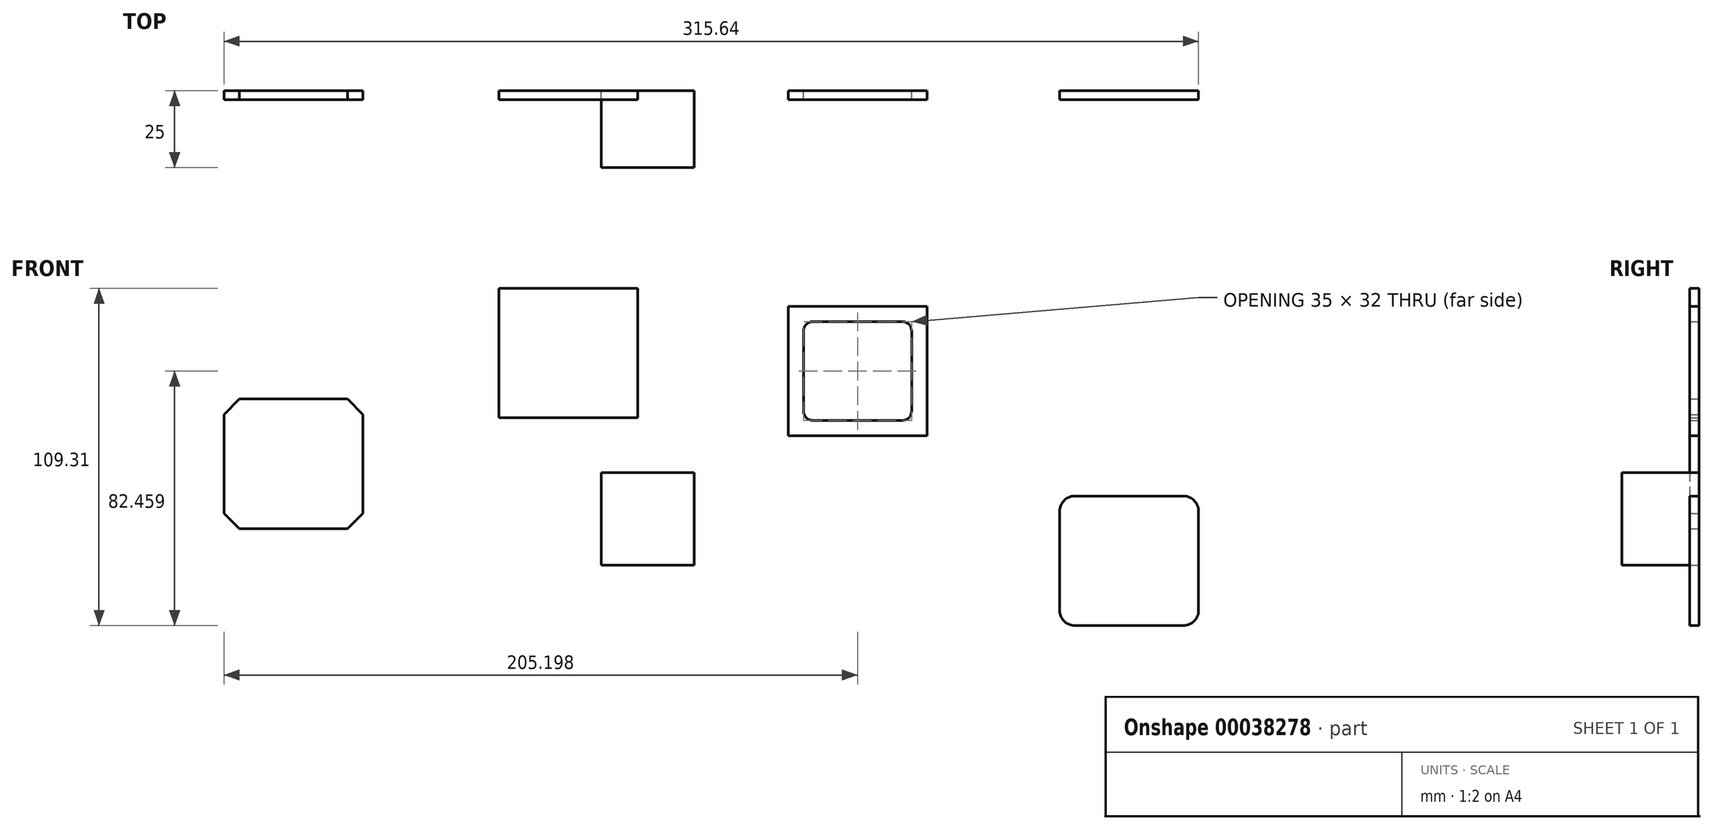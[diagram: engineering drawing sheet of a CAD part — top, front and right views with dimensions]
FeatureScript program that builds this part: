
annotation { "Feature Type Name" : "Feature", "Feature Type Description" : "" }
export const myFeature = defineFeature(function(context is Context, id is Id, definition is map)
    precondition{}
    {
        {
            var Q0;
            Q0=qCreatedBy(makeId("Front.planeOp"),FACE);
            var sketch = newSketch(context, id + "F0", { "sketchPlane" : qUnion([Q0])});
            skLineSegment(sketch, "E0.bottom", {"start": v(-81.03, 57.95) * mm, "end": v(-36.03, 57.95) * mm});
            skLineSegment(sketch, "E0.top", {"start": v(-81.03, 15.95) * mm, "end": v(-36.03, 15.95) * mm});
            skLineSegment(sketch, "E0.left", {"start": v(-81.03, 57.95) * mm, "end": v(-81.03, 15.95) * mm});
            skLineSegment(sketch, "E0.right", {"start": v(-36.03, 57.95) * mm, "end": v(-36.03, 15.95) * mm});
            skSolve(sketch);
        }
        {
            var Q0;
            Q0 = qSketchRegion(id + "F0", true);
            extrude(context, id + "F1", {"entities" : qUnion([Q0]), "depth" : 3 * mm});
        }
        {
            var Q0;
            Q0=qCreatedBy(makeId("Front.planeOp"),FACE);
            var sketch = newSketch(context, id + "F2", { "sketchPlane" : qUnion([Q0])});
            skLineSegment(sketch, "E1.bottom", {"start": v(12.66, 52.1) * mm, "end": v(57.66, 52.1) * mm});
            skLineSegment(sketch, "E1.top", {"start": v(12.66, 10.1) * mm, "end": v(57.66, 10.1) * mm});
            skLineSegment(sketch, "E1.left", {"start": v(12.66, 52.1) * mm, "end": v(12.66, 10.1) * mm});
            skLineSegment(sketch, "E1.right", {"start": v(57.66, 52.1) * mm, "end": v(57.66, 10.1) * mm});
            skLineSegment(sketch, "E2.rect.bottom", {"start": v(49.66, 47.1) * mm, "end": v(20.66, 47.1) * mm});
            skLineSegment(sketch, "E2.rect.top", {"start": v(49.66, 15.1) * mm, "end": v(20.66, 15.1) * mm});
            skLineSegment(sketch, "E2.rect.left", {"start": v(52.66, 44.1) * mm, "end": v(52.66, 18.1) * mm});
            skLineSegment(sketch, "E2.rect.right", {"start": v(17.66, 44.1) * mm, "end": v(17.66, 18.1) * mm});
            skPoint(sketch, "E2.rect.middle", {"position": v(35.16, 31.1) * mm});
            skPoint(sketch, "E2.rect.middle.positionSnap0", {"position": v(35.16, 52.1) * mm});
            skPoint(sketch, "E2.rect.middle.positionSnap1", {"position": v(57.66, 31.1) * mm});
            skPoint(sketch, "E2.rect.centerSnap0", {"position": v(35.16, 52.1) * mm});
            skPoint(sketch, "E2.rect.centerSnap1", {"position": v(57.66, 31.1) * mm});
            skPoint(sketch, "E3.visualSharp", {"position": v(17.66, 47.1) * mm});
            skArc(sketch, "E3.filletArc", {"start": v(20.66, 47.1) * mm, "mid": v(18.54, 46.22) * mm, "end": v(17.66, 44.1) * mm});
            skPoint(sketch, "E4.visualSharp", {"position": v(52.66, 47.1) * mm});
            skArc(sketch, "E4.filletArc", {"start": v(52.66, 44.1) * mm, "mid": v(51.78, 46.22) * mm, "end": v(49.66, 47.1) * mm});
            skPoint(sketch, "E5.visualSharp", {"position": v(52.66, 15.1) * mm});
            skArc(sketch, "E5.filletArc", {"start": v(49.66, 15.1) * mm, "mid": v(51.78, 15.98) * mm, "end": v(52.66, 18.1) * mm});
            skPoint(sketch, "E6.visualSharp", {"position": v(17.66, 15.1) * mm});
            skArc(sketch, "E6.filletArc", {"start": v(17.66, 18.1) * mm, "mid": v(18.54, 15.98) * mm, "end": v(20.66, 15.1) * mm});
            skSolve(sketch);
        }
        {
            var Q0;
            Q0 = qSketchRegion(id + "F2", true);
            extrude(context, id + "F3", {"entities" : qUnion([Q0]), "depth" : 3 * mm});
        }
        {
            var Q0;
            Q0=qCreatedBy(makeId("Front.planeOp"),FACE);
            var sketch = newSketch(context, id + "F4", { "sketchPlane" : qUnion([Q0])});
            skLineSegment(sketch, "E7.bottom", {"start": v(-47.83, -1.77) * mm, "end": v(-17.83, -1.77) * mm});
            skLineSegment(sketch, "E7.top", {"start": v(-47.83, -31.77) * mm, "end": v(-17.83, -31.77) * mm});
            skLineSegment(sketch, "E7.left", {"start": v(-47.83, -1.77) * mm, "end": v(-47.83, -31.77) * mm});
            skLineSegment(sketch, "E7.right", {"start": v(-17.83, -1.77) * mm, "end": v(-17.83, -31.77) * mm});
            skSolve(sketch);
        }
        {
            var Q0;
            Q0 = qSketchRegion(id + "F4", true);
            extrude(context, id + "F5", {"entities" : qUnion([Q0]), "depth" : 25 * mm});
        }
        {
            var Q0;
            Q0=qCreatedBy(makeId("Front.planeOp"),FACE);
            var sketch = newSketch(context, id + "F6", { "sketchPlane" : qUnion([Q0])});
            skLineSegment(sketch, "E8.bottom", {"start": v(105.6, -9.36) * mm, "end": v(140.6, -9.36) * mm});
            skLineSegment(sketch, "E8.top", {"start": v(105.6, -51.36) * mm, "end": v(140.6, -51.36) * mm});
            skLineSegment(sketch, "E8.left", {"start": v(100.6, -14.36) * mm, "end": v(100.6, -46.36) * mm});
            skLineSegment(sketch, "E8.right", {"start": v(145.6, -14.36) * mm, "end": v(145.6, -46.36) * mm});
            skPoint(sketch, "E9.visualSharp", {"position": v(100.6, -9.36) * mm});
            skArc(sketch, "E9.filletArc", {"start": v(105.6, -9.36) * mm, "mid": v(102.06, -10.82) * mm, "end": v(100.6, -14.36) * mm});
            skPoint(sketch, "E10.visualSharp", {"position": v(145.6, -9.36) * mm});
            skArc(sketch, "E10.filletArc", {"start": v(145.6, -14.36) * mm, "mid": v(144.13, -10.82) * mm, "end": v(140.6, -9.36) * mm});
            skPoint(sketch, "E11.visualSharp", {"position": v(145.6, -51.36) * mm});
            skArc(sketch, "E11.filletArc", {"start": v(140.6, -51.36) * mm, "mid": v(144.13, -49.9) * mm, "end": v(145.6, -46.36) * mm});
            skPoint(sketch, "E12.visualSharp", {"position": v(100.6, -51.36) * mm});
            skArc(sketch, "E12.filletArc", {"start": v(100.6, -46.36) * mm, "mid": v(102.06, -49.9) * mm, "end": v(105.6, -51.36) * mm});
            skSolve(sketch);
        }
        {
            var Q0;
            Q0=makeQuery(id+"F6.imprint","IMPRINT",FACE,{"disambiguationData":[TD([[makeQuery(id+"F6.imprint","IMPRINT",EDGE,{"derivedFrom":sQuery(id+"F6.wireOp",EDGE,"E8.bottom")}),-1.0]])]});
            extrude(context, id + "F7", {"entities" : qUnion([Q0]), "depth" : 3 * mm});
        }
        {
            var Q0;
            Q0=qCreatedBy(makeId("Front.planeOp"),FACE);
            var sketch = newSketch(context, id + "F8", { "sketchPlane" : qUnion([Q0])});
            skLineSegment(sketch, "E13", {"start": v(-165.04, 22.04) * mm, "end": v(-130.04, 22.04) * mm});
            skLineSegment(sketch, "E14", {"start": v(-170.04, 17.04) * mm, "end": v(-170.04, -14.96) * mm});
            skLineSegment(sketch, "E15", {"start": v(-125.04, 17.04) * mm, "end": v(-125.04, -14.96) * mm});
            skLineSegment(sketch, "E16", {"start": v(-165.04, -19.96) * mm, "end": v(-130.04, -19.96) * mm});
            skLineSegment(sketch, "E17", {"start": v(-170.04, 17.04) * mm, "end": v(-165.04, 22.04) * mm});
            skLineSegment(sketch, "E18", {"start": v(-130.04, 22.04) * mm, "end": v(-125.04, 17.04) * mm});
            skLineSegment(sketch, "E19", {"start": v(-125.04, -14.96) * mm, "end": v(-130.04, -19.96) * mm});
            skLineSegment(sketch, "E20", {"start": v(-165.04, -19.96) * mm, "end": v(-170.04, -14.96) * mm});
            skSolve(sketch);
        }
        {
            var Q0;
            Q0 = qSketchRegion(id + "F8", true);
            extrude(context, id + "F9", {"entities" : qUnion([Q0]), "depth" : 3 * mm});
        }
    });
